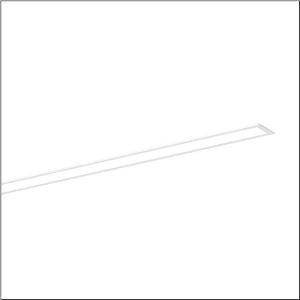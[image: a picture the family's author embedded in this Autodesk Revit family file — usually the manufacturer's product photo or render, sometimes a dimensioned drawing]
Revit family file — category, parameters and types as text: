
# Revit family: silica_r__21_51mx10da32wb_2fdc
name_source: partatom
category: Lighting Fixtures
units: mm (PartAtom-declared; Revit-internal decimal feet)

## family parameters
Cut with Voids When Loaded = No
Host = Face
Light Source = No
Part Type = Normal
Room Calculation Point = No
Round Connector Dimension = Use Diameter
Shared = No

## types (1)
- --- (1 x LED, 2400 lm, 16.1 W, 3000K)
    Apparent Load = 16 VA
    CIE Flux Codes = 48 79 96 100 100
    Color Rendering = 80
    Color Temperature = 3000K
    Default Elevation = 1800 mm
    Description = Silica® 21, office luminaire, primary optical cover: cover, of PMMA, opal, light emission: direct distribution, primary light characteristic: symmetric, installation type: recessed, LED, rated luminous flux: 2.400lm, luminous efficacy: 149lm/W, light colour: 830, colour temperature: 3000K, with terminal, 3+2-pole, max. 2.5mm², mains connection: 220..240V, AC, 50/60Hz, rated input power: 16.1W, luminaire housing, of aluminium, traffic white (RAL 9016), length: 1.228mm, width: 79mm, height: 53mm, protection rating (complete): IP20, insulation class (complete): insulation class I (protective earthing), certification: CE, permissible operating ambient temperature: 0..+35°C, standard: EN 50419, packaging unit: 1 piece
    Height = 0 mm  [stored 0 ft]
    Lamp = 1 x LED
    Lamp Light Flux = 2400 lm
    Lamp Power = 16.1 W
    Lamp count = 1
    Length = 1227 mm
    Luminous efficacy = 149 lm/W
    Manufacturer = Siteco
    ModVariant = No
    Model = 51MX10DA32WB
    Mounting Place = Ceiling
    Mounting Type = Recessed
    Number of Poles = 1
    OnlyDefault = Yes
    Power Factor = 1
    Product Name = Silica® 21
    Product group = office luminaire | ceiling recessed
    ProductGroupID = 401
    Protection Class = Protection class I
    Protection Degree = IP 20
    RLX_Detail_Level = 1
    RLX_Emergency_Light_Flux = 0 lm
    RLX_Emergency_Type = 0
    RLX_Emergency_Type_DB = No
    RlxData = <blob elided: 20981 chars, md5=15bc2d6f>
    Socket = socket
    Standby Power = 0 W
    System Light Flux = 2400 lm
    System Power = 16 W
    Type Comments = factory setting: luminous flux: 100 % | dim-lin: 254 | 233 mA
    Type Image = l_1313615.jpg
    URL = http://relux.com
    VarID = @adj_065915
    Voltage = 0 V
    Weight = 0.00 kg
    Width = 79 mm

note: [stored X ft] marks values corroborated as IEEE doubles in the binary element streams (Revit-internal decimal feet)

## geometry (parser evidence)
native form markers: Blend x4, Sweep x11
no freeform markers — native parametric forms only
